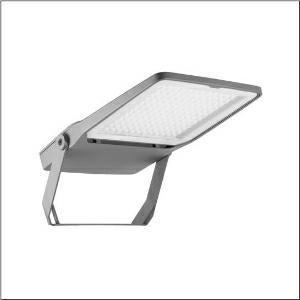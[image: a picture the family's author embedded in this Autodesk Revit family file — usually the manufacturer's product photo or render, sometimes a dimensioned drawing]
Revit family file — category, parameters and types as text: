
# Revit family: floodlight_fl_20_midi___pl52_5xa7682e1d1ac_f3ed
name_source: partatom
category: Lighting Fixtures
units: mm (PartAtom-declared; Revit-internal decimal feet)

## family parameters
Cut with Voids When Loaded = No
Host = Face
Light Source = No
Part Type = Normal
Room Calculation Point = No
Round Connector Dimension = Use Diameter
Shared = No

## types (1)
- --- (1 x LED 3000K / CRI = 80 (unbekannt), 21030 lm, 3000K)
    Apparent Load = 208 VA
    CIE Flux Codes = 27 59 98 100 100
    Color Rendering = 80
    Color Temperature = 3000K
    Default Elevation = 1800 mm
    Description = Floodlight FL 20 midi, floodlight, primary light control with lens, of plastic, primary optical cover: protective disc, of toughened safety glass, transparent, light distribution: PL52, light emission: direct distribution, primary light characteristic: asymmetric, installation type: surface-mounted, LED High Power LED, rated luminous flux: 21.030 lm, light colour: 830, colour temperature: 3000K, control gear: ECG Plus, control: flexible luminous flux parameterisation, time-dependent luminous flux control, digital communication interface, power reduction, overheat protection, electronic power reduction, with terminal, 5-pole, max. 2.5mm², mains connection: 220..240V, AC, 50/60Hz, rated input power: 208W, LED unit, of diecast aluminium, powder-coated, Siteco® metallic grey (DB 702S), length: 654 mm, width: 450 mm, height: 76mm, housing frame, of diecast aluminium, powder-coated, Siteco® metallic grey (DB 702S), mounting bracket, of steel, powder-coated, Siteco® metallic grey (DB 702S), DALIprotection rating (complete): IP66, insulation class (complete): insulation class II (safety insulation), certification: CE, ENEC, VDE, protection symbol: D, permissible ambient temperature for indoor applications: -40..+40°C, permissible ambient temperature for outdoor applications: -40..+50°C, standard: DIN EN 12944, packaging unit: 1 piece

Light Distribution: PL52
    Height = 76 mm
    Lamp = 1 x LED 3000K / CRI >= 80 (unbekannt)
    Lamp Light Flux = 21030 lm
    Lamp count = 1
    Length = 672 mm
    Luminous efficacy = 101 lm/W
    Manufacturer = Siteco
    ModVariant = No
    Model = 5XA7682E1D1AC
    Number of Poles = 1
    OnlyDefault = Yes
    Power Factor = 1
    Product Name = Floodlight FL 20 midi | PL52
    Product group = floodlight | pylon top
    ProductGroupID = 6101
    Protection Class = Protection class II
    Protection Degree = IP 66
    RLX_Detail_Level = 1
    RlxData = <blob elided: 97793 chars, md5=0294a60b>
    Socket = socket
    Standby Power = 0 W
    System Light Flux = 21030 lm
    System Power = 208 W
    Type Comments = factory setting: luminous flux: 100 % | dim-lin: 254 | 484 mA
    Type Image = l_1005943.jpg
    URL = http://relux.com
    VarID = @adj_143079
    Voltage = 0 V
    Weight = 0.00 kg
    Width = 450 mm

## geometry (parser evidence)
native form markers: Blend x4, Sweep x10
no freeform markers — native parametric forms only
